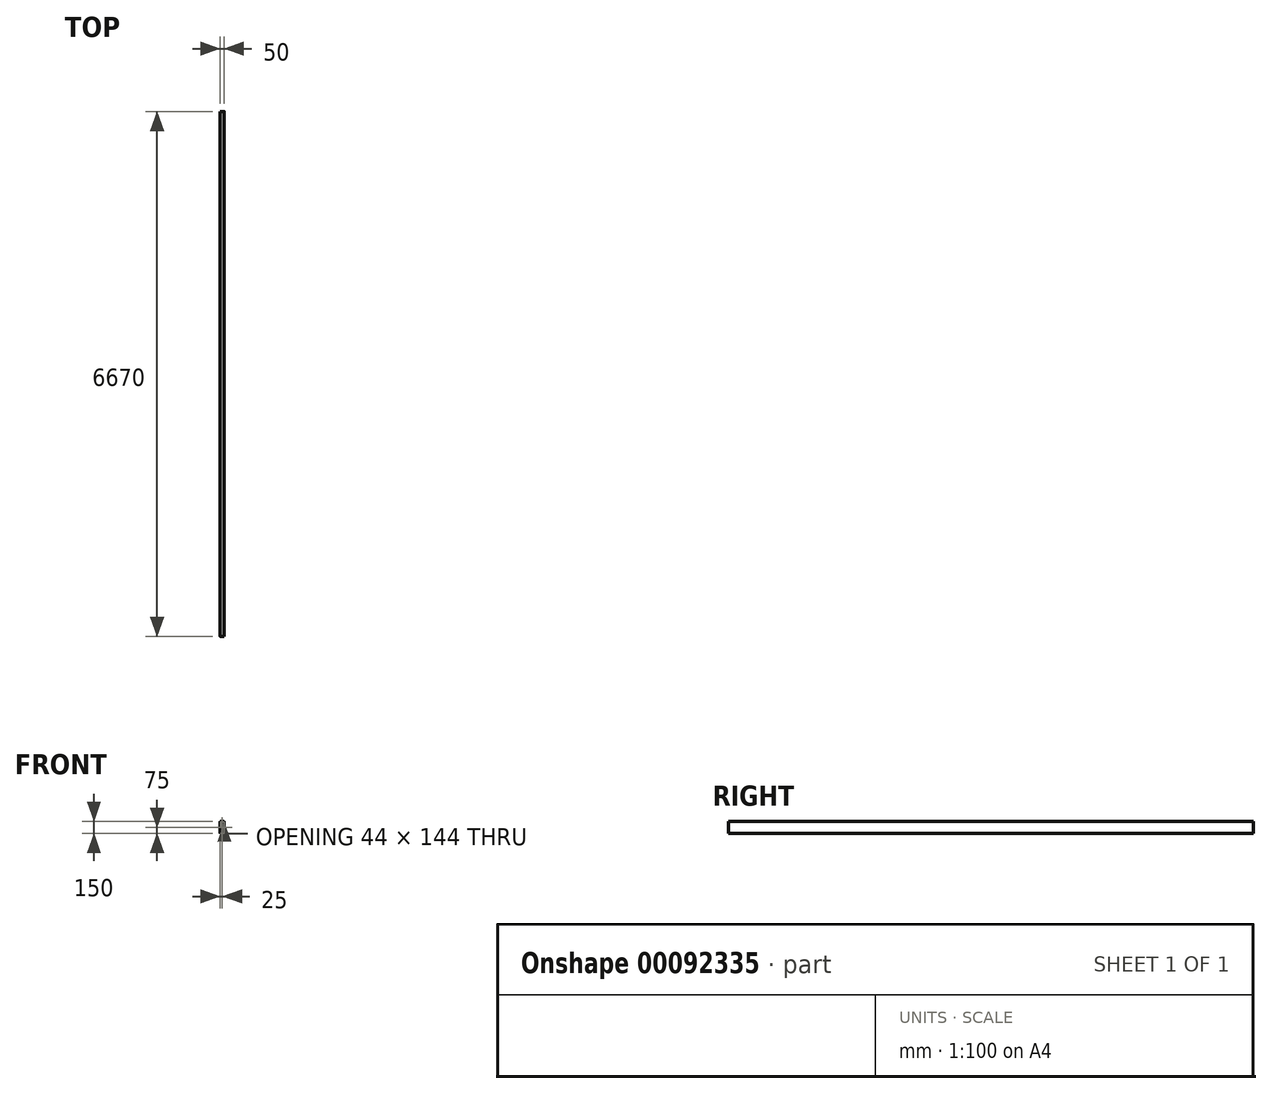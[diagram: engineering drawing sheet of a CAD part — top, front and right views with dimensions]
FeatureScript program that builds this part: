
annotation { "Feature Type Name" : "Feature", "Feature Type Description" : "" }
export const myFeature = defineFeature(function(context is Context, id is Id, definition is map)
    precondition{}
    {
        {
            var Q0;
            Q0=qCreatedBy(makeId("Front.planeOp"),FACE);
            var sketch = newSketch(context, id + "F0", { "sketchPlane" : qUnion([Q0])});
            skLineSegment(sketch, "E0.bottom", {"start": v(2.4, 0) * mm, "end": v(47.6, 0) * mm});
            skLineSegment(sketch, "E0.top", {"start": v(2.4, 150) * mm, "end": v(47.6, 150) * mm});
            skLineSegment(sketch, "E0.left", {"start": v(0, 2.4) * mm, "end": v(0, 147.6) * mm});
            skLineSegment(sketch, "E0.right", {"start": v(50, 2.4) * mm, "end": v(50, 147.6) * mm});
            skPoint(sketch, "E1.visualSharp", {"position": v(0, 150) * mm});
            skArc(sketch, "E1.filletArc", {"start": v(2.4, 150) * mm, "mid": v(0.7, 149.3) * mm, "end": v(0, 147.6) * mm});
            skPoint(sketch, "E2.visualSharp", {"position": v(50, 150) * mm});
            skArc(sketch, "E2.filletArc", {"start": v(50, 147.6) * mm, "mid": v(49.3, 149.3) * mm, "end": v(47.6, 150) * mm});
            skPoint(sketch, "E3.visualSharp", {"position": v(0, 0) * mm});
            skArc(sketch, "E3.filletArc", {"start": v(0, 2.4) * mm, "mid": v(0.7, 0.7) * mm, "end": v(2.4, 0) * mm});
            skPoint(sketch, "E4.visualSharp", {"position": v(50, 0) * mm});
            skArc(sketch, "E4.filletArc", {"start": v(47.6, 0) * mm, "mid": v(49.3, 0.7) * mm, "end": v(50, 2.4) * mm});
            skLineSegment(sketch, "E5.0", {"start": v(3, 5.4) * mm, "end": v(3, 144.6) * mm});
            skLineSegment(sketch, "E6.0", {"start": v(5.4, 147) * mm, "end": v(44.6, 147) * mm});
            skLineSegment(sketch, "E7.0", {"start": v(47, 5.4) * mm, "end": v(47, 144.6) * mm});
            skLineSegment(sketch, "E8.0", {"start": v(5.4, 3) * mm, "end": v(44.6, 3) * mm});
            skArc(sketch, "E9.filletArc", {"start": v(5.4, 147) * mm, "mid": v(3.7, 146.3) * mm, "end": v(3, 144.6) * mm});
            skArc(sketch, "E10.filletArc", {"start": v(3, 5.4) * mm, "mid": v(3.7, 3.7) * mm, "end": v(5.4, 3) * mm});
            skArc(sketch, "E11.filletArc", {"start": v(47, 144.6) * mm, "mid": v(46.3, 146.3) * mm, "end": v(44.6, 147) * mm});
            skArc(sketch, "E12.filletArc", {"start": v(44.6, 3) * mm, "mid": v(46.3, 3.7) * mm, "end": v(47, 5.4) * mm});
            skSolve(sketch);
        }
        {
            var Q0;
            Q0=qSketchRegion(id+"F0",true);
            extrude(context, id + "F1", {"entities" : qUnion([Q0]), "depth" : 6670 * mm, "offsetDistance" : 25 * mm});
        }
    });
